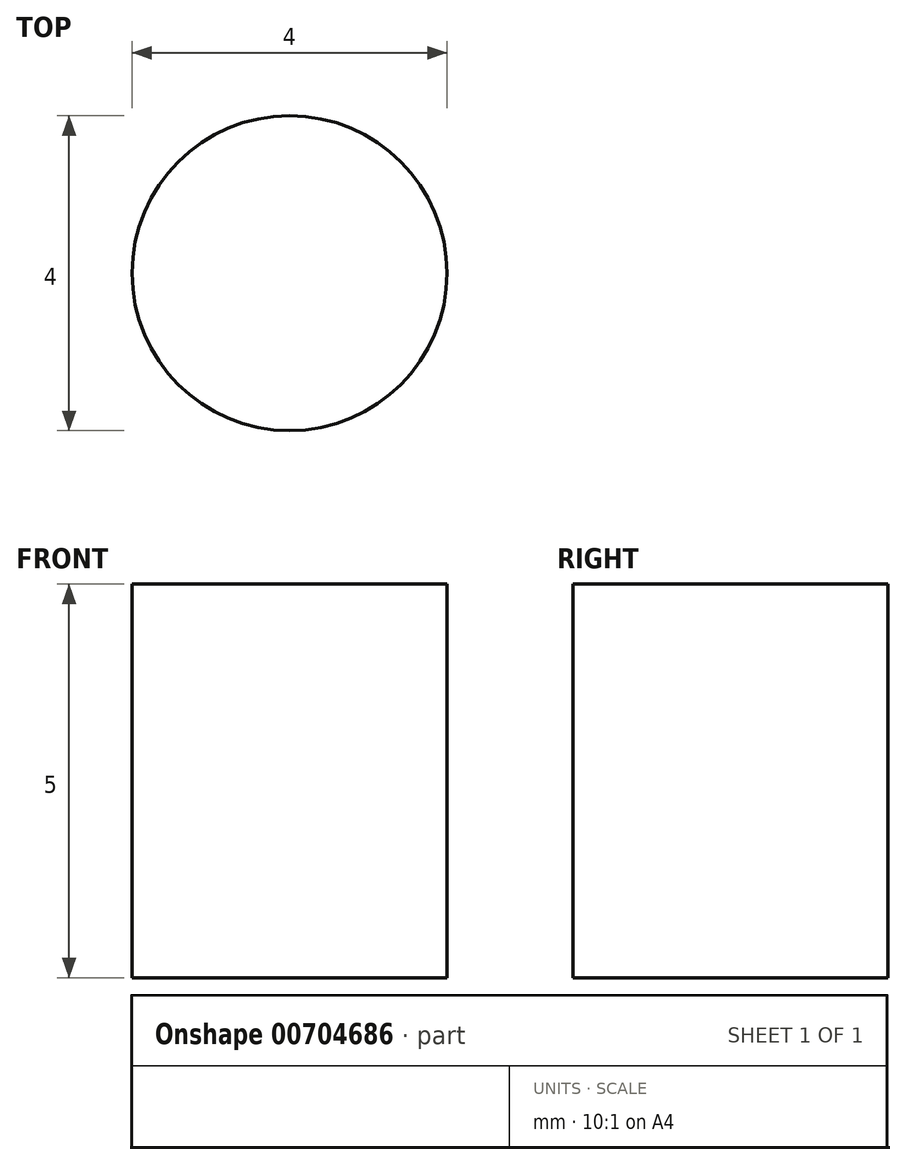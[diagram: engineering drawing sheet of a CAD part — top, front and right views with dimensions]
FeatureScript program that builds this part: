
annotation { "Feature Type Name" : "Feature", "Feature Type Description" : "" }
export const myFeature = defineFeature(function(context is Context, id is Id, definition is map)
    precondition{}
    {
        {
            var Q0;
            Q0=qCreatedBy(makeId("Top.planeOp"),FACE);
            var sketch = newSketch(context, id + "F0", { "sketchPlane" : qUnion([Q0])});
            skCircle(sketch, "E0", {"center": v(0, 0) * mm, "radius": 2 * mm});
            skSolve(sketch);
        }
        {
            var Q0;
            Q0=makeQuery(id+"F0.imprint","IMPRINT",FACE,{"disambiguationData":[TD([[makeQuery(id+"F0.imprint","IMPRINT",EDGE,{"derivedFrom":sQuery(id+"F0.wireOp",EDGE,"E0")}),1.0]])]});
            extrude(context, id + "F1", {"entities" : qUnion([Q0]), "depth" : 5 * mm, "offsetDistance" : 25 * mm});
        }
    });
